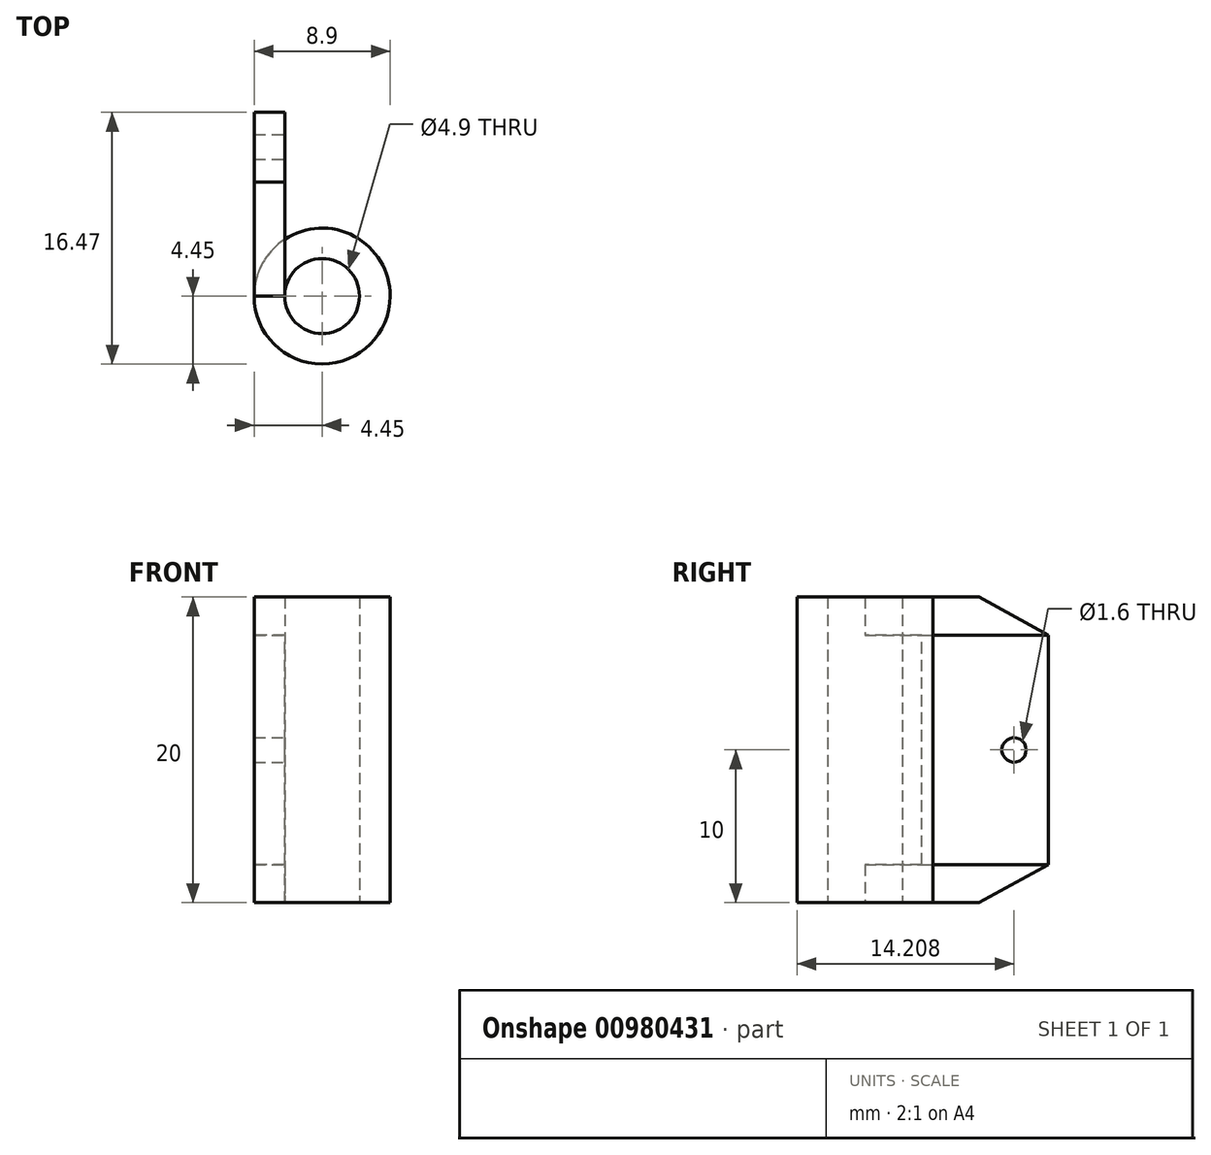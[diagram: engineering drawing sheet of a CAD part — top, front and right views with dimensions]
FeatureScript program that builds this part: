
annotation { "Feature Type Name" : "Feature", "Feature Type Description" : "" }
export const myFeature = defineFeature(function(context is Context, id is Id, definition is map)
    precondition{}
    {
        {
            var Q0;
            Q0=qCreatedBy(makeId("Top.planeOp"),FACE);
            var sketch = newSketch(context, id + "F0", { "sketchPlane" : qUnion([Q0])});
            skCircle(sketch, "E0", {"center": v(0, 0) * mm, "radius": 2.45 * mm});
            skCircle(sketch, "E1", {"center": v(0, 0) * mm, "radius": 4.45 * mm});
            skLineSegment(sketch, "E2", {"start": v(-2.45, 0) * mm, "end": v(-2.45, 12) * mm});
            skLineSegment(sketch, "E3", {"start": v(-4.45, 0) * mm, "end": v(-4.45, 12.02) * mm});
            skLineSegment(sketch, "E4", {"start": v(-4.45, 12.02) * mm, "end": v(-2.45, 12) * mm});
            skPoint(sketch, "E5", {"position": v(0, 12) * mm});
            skSolve(sketch);
        }
        {
            var Q0;
            {var subQ0=sQuery(id+"F0.wireOp",EDGE,"E3");Q0=makeQuery(id+"F0.imprint","IMPRINT",FACE,{"disambiguationData":[TD([[makeQuery(id+"F0.imprint","IMPRINT",EDGE,{"derivedFrom":subQ0}),-1.0]])]});}
            extrude(context, id + "F1", {"entities" : qUnion([Q0]), "endBound" : BoundingType.SYMMETRIC, "oppositeDirection" : true, "depth" : 15 * mm, "offsetDistance" : 25 * mm});
        }
        {
            var Q0;
            Q0=makeQuery(id+"F0.imprint","IMPRINT",FACE,{"disambiguationData":[TD([[makeQuery(id+"F0.imprint","IMPRINT",EDGE,{"derivedFrom":sQuery(id+"F0.wireOp",EDGE,"E0")}),-1.0]])]});
            extrude(context, id + "F2", {"entities" : qUnion([Q0]), "operationType" : NewBodyOperationType.ADD, "endBound" : BoundingType.SYMMETRIC, "depth" : 20 * mm, "offsetDistance" : 25 * mm});
        }
        {
            var Q0;
            Q0=makeQuery(id+"F1.opExtrude","SWEPT_FACE",FACE,{"disambiguationData":[OSD([sQuery(id+"F0.wireOp",EDGE,"E2")])]});
            var sketch = newSketch(context, id + "F3", { "sketchPlane" : qUnion([Q0])});
            skPoint(sketch, "E6", {"position": v(9.76, 0) * mm});
            skSolve(sketch);
        }
        {
            var Q0;
            Q0=sQuery(id+"F3.wireOp",VERTEX,"E6");
            var Q1;
            Q1=makeQuery(id+"F1.opExtrude","SWEPT_BODY",BODY,{"disambiguationData":[OSD([sQuery(id+"F0.wireOp",EDGE,"E1"),sQuery(id+"F0.wireOp",EDGE,"E2"),sQuery(id+"F0.wireOp",EDGE,"E3"),sQuery(id+"F0.wireOp",EDGE,"E4")])]});
            hole(context, id + "F4", {"style" : HoleStyle.SIMPLE, "endStyle" : HoleEndStyle.BLIND, "standardTappedOrClearance" : lookupTablePath({ "fit" : "Normal", "standard" : "ISO", "size" : "M1.4", "type" : "Clearance" }), "standardBlindInLast" : lookupTablePath({ "fit" : "Normal", "standard" : "ISO", "engagement" : "75%", "pitch" : "0.2 mm", "size" : "M1.4", "type" : "Clearance & tapped" }), "holeDiameter" : 1.6 * mm, "majorDiameter" : 5 * mm, "holeDepth" : 20 * mm, "isTappedThrough" : true, "tappedDepth" : 12 * mm, "tapClearance" : 3, "locations" : qUnion([Q0]), "scope" : qUnion([Q1])});
        }
        {
            var Q0;
            Q0=makeQuery(id+"F1.opExtrude","SWEPT_FACE",FACE,{"disambiguationData":[OSD([sQuery(id+"F0.wireOp",EDGE,"E3")])]});
            var sketch = newSketch(context, id + "F5", { "sketchPlane" : qUnion([Q0])});
            skLineSegment(sketch, "E7", {"start": v(0, 9.99) * mm, "end": v(0, -10) * mm});
            skLineSegment(sketch, "E8", {"start": v(-12.02, -7.5) * mm, "end": v(-12.02, 7.5) * mm});
            skLineSegment(sketch, "E9", {"start": v(-7.48, -10) * mm, "end": v(-12.02, -7.5) * mm});
            skLineSegment(sketch, "E10", {"start": v(-7.48, -10) * mm, "end": v(0, -10) * mm});
            skLineSegment(sketch, "E11.MirrorCS", {"start": v(-7.48, 10) * mm, "end": v(-12.02, 7.5) * mm});
            skLineSegment(sketch, "E12.MirrorCS", {"start": v(-7.48, 10) * mm, "end": v(0, 10) * mm});
            skLineSegment(sketch, "E13.MirrorCS", {"start": v(0, -9.99) * mm, "end": v(0, 10) * mm});
            skLineSegment(sketch, "E14.MirrorCS", {"start": v(-12.02, 7.5) * mm, "end": v(-12.02, -7.5) * mm});
            skSolve(sketch);
        }
        {
            var Q0;
            {var subQ2=sQuery(id+"F5.wireOp",EDGE,"E7");Q0=makeQuery(id+"F5.imprint","IMPRINT",FACE,{"disambiguationData":[TD([[makeQuery(id+"F5.imprint","IMPRINT",EDGE,{"derivedFrom":subQ2}),-1.0]])]});}
            var Q1;
            Q1=makeQuery(id+"F5.imprint","IMPRINT",FACE,{"disambiguationData":[TD([[makeQuery(id+"F5.imprint","IMPRINT",EDGE,{"derivedFrom":sQuery(id+"F5.wireOp",EDGE,"E11.MirrorCS")}),1.0]])]});
            extrude(context, id + "F6", {"entities" : qUnion([Q0, Q1]), "oppositeDirection" : true, "depth" : 2 * mm, "offsetDistance" : 25 * mm});
        }
    });
